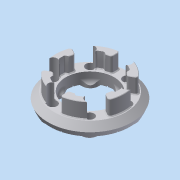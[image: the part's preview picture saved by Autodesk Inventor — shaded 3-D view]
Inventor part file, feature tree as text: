
AUTODESK INVENTOR PART (.ipt)
format: ipt  version: 2014 SP1 (Build 180222100, 222)  size: 816,640 bytes
history: native  units: in
note: dims shown in document units (in); Inventor stores cm internally (conversion verified against a paired STEP export)
features: sketch x5, other x3
ambient origin geometry x8: Origin, YZ Plane, XZ Plane, XY Plane, X Axis, Y Axis, Z Axis, Center Point
bodies: Solid1 (feature_tree)
feature tree (8):
  other  "wheelinsertouter.ipt"
  other  "Solid1::wheelinsertouter.ipt"
  other  "TaggingFeature1"
  sketch  "Sketch1"  dims[d0=0.3937in]
  sketch  "Sketch5"  dims[d1=0.35in d2=0.0in d3=2.15in d4=0.25in d5=0.0in d6=0.25in d42=0.1625in d46=0.0in d47=0.375in d48=0.375in d49=0.375in d50=0.375in d51=0.375in d52=0.375in d53=0.01in d54=0.0in d67=0.01in d68=0.01in d69=2.3622in d73=0.02in d74=0.0in d78=0.047in d81=0.15in d82=0.145in d83=0.05in d84=0.0in d85=0.05in d88=0.0197in d89=0.0197in d90=0.0in d91=0.0197in d94=0.0098in d97=2.0in d98=2.3622in d99=360.0deg d71=360.0deg]
  sketch  "Sketch8"
  sketch  "Sketch6"
  sketch  "Sketch9"
